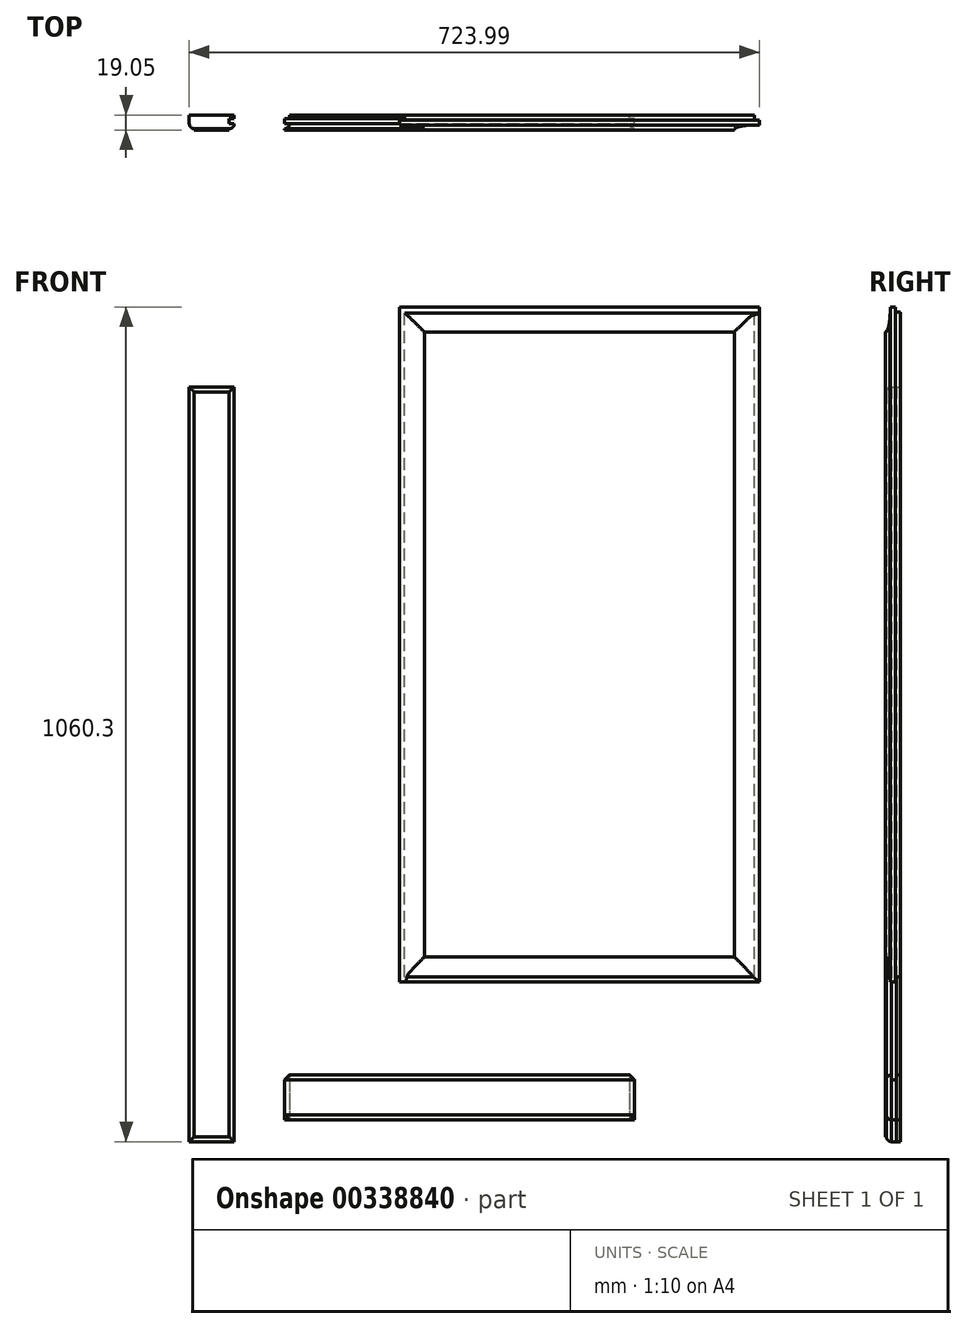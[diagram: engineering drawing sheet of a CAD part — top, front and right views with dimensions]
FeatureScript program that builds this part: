
annotation { "Feature Type Name" : "Feature", "Feature Type Description" : "" }
export const myFeature = defineFeature(function(context is Context, id is Id, definition is map)
    precondition{}
    {
        {
            var Q0;
            Q0=qCreatedBy(makeId("Front.planeOp"),FACE);
            var sketch = newSketch(context, id + "F0", { "sketchPlane" : qUnion([Q0])});
            skLineSegment(sketch, "E0.bottom", {"start": v(-96.9, 637.81) * mm, "end": v(-39.75, 637.81) * mm});
            skLineSegment(sketch, "E0.top", {"start": v(-96.9, -321.04) * mm, "end": v(-39.75, -321.04) * mm});
            skLineSegment(sketch, "E0.left", {"start": v(-96.9, 637.81) * mm, "end": v(-96.9, -321.04) * mm});
            skLineSegment(sketch, "E0.right", {"start": v(-39.75, 637.81) * mm, "end": v(-39.75, -321.04) * mm});
            skSolve(sketch);
        }
        {
            var Q0;
            Q0 = qSketchRegion(id + "F0", true);
            extrude(context, id + "F1", {"entities" : qUnion([Q0]), "depth" : 19.05 * mm});
        }
        {
            var Q0;
            Q0=makeQuery(id+"F1.opExtrude","SWEPT_FACE",FACE,{"disambiguationData":[OSD([sQuery(id+"F0.wireOp",EDGE,"E0.top")])]});
            var sketch = newSketch(context, id + "F2", { "sketchPlane" : qUnion([Q0])});
            skLineSegment(sketch, "E1.0", {"start": v(-46.1, 19.05) * mm, "end": v(-46.1, 0) * mm, "construction": true});
            skLineSegment(sketch, "E2.0", {"start": v(-96.9, 17.46) * mm, "end": v(-39.75, 17.46) * mm, "construction": true});
            skLineSegment(sketch, "E3.0", {"start": v(-96.9, 11.11) * mm, "end": v(-39.75, 11.11) * mm, "construction": true});
            skArc(sketch, "E4", {"start": v(-39.75, 11.11) * mm, "mid": v(-41.6, 15.6) * mm, "end": v(-46.1, 17.46) * mm});
            skLineSegment(sketch, "E5", {"start": v(-46.1, 19.05) * mm, "end": v(-46.1, 17.46) * mm});
            skLineSegment(sketch, "E6.0", {"start": v(-96.9, 4.76) * mm, "end": v(-39.75, 4.76) * mm, "construction": true});
            skLineSegment(sketch, "E7", {"start": v(-39.75, 11.11) * mm, "end": v(-46.1, 11.11) * mm});
            skLineSegment(sketch, "E8", {"start": v(-46.1, 4.76) * mm, "end": v(-39.75, 4.76) * mm});
            skLineSegment(sketch, "E9", {"start": v(-46.1, 4.76) * mm, "end": v(-46.1, 11.11) * mm});
            skLineSegment(sketch, "E10.0", {"start": v(-90.55, 19.05) * mm, "end": v(-90.55, 0) * mm, "construction": true});
            skArc(sketch, "E11", {"start": v(-90.55, 17.46) * mm, "mid": v(-95.04, 15.6) * mm, "end": v(-96.9, 11.11) * mm});
            skLineSegment(sketch, "E12", {"start": v(-90.55, 17.46) * mm, "end": v(-90.55, 19.05) * mm});
            skSolve(sketch);
        }
        {
            var Q0;
            {var subQ0=sQuery(id+"F2.wireOp",EDGE,"E4");Q0=makeQuery(id+"F2.imprint","IMPRINT",FACE,{"disambiguationData":[TD([[makeQuery(id+"F2.imprint","IMPRINT",EDGE,{"derivedFrom":subQ0}),-1.0]])]});}
            extrude(context, id + "F3", {"entities" : qUnion([Q0]), "operationType" : NewBodyOperationType.REMOVE, "oppositeDirection" : true, "depth" : 965.2 * mm});
        }
        {
            var Q0;
            {var subQ0=sQuery(id+"F2.wireOp",EDGE,"E7");Q0=makeQuery(id+"F2.imprint","IMPRINT",FACE,{"disambiguationData":[TD([[makeQuery(id+"F2.imprint","IMPRINT",EDGE,{"derivedFrom":subQ0}),1.0]])]});}
            extrude(context, id + "F4", {"entities" : qUnion([Q0]), "operationType" : NewBodyOperationType.REMOVE, "oppositeDirection" : true, "depth" : 965.2 * mm});
        }
        {
            var Q0;
            {var subQ0=sQuery(id+"F2.wireOp",EDGE,"E11");Q0=makeQuery(id+"F2.imprint","IMPRINT",FACE,{"disambiguationData":[TD([[makeQuery(id+"F2.imprint","IMPRINT",EDGE,{"derivedFrom":subQ0}),-1.0]])]});}
            extrude(context, id + "F5", {"entities" : qUnion([Q0]), "operationType" : NewBodyOperationType.REMOVE, "oppositeDirection" : true, "depth" : 965.2 * mm});
        }
        {
            var Q0;
            Q0=makeQuery(id+"F1.opExtrude","SWEPT_FACE",FACE,{"disambiguationData":[OSD([sQuery(id+"F0.wireOp",EDGE,"E0.left")])]});
            var sketch = newSketch(context, id + "F6", { "sketchPlane" : qUnion([Q0])});
            skLineSegment(sketch, "E13.0", {"start": v(17.46, -314.69) * mm, "end": v(0, -314.69) * mm, "construction": true});
            skArc(sketch, "E14", {"start": v(11.11, -321.04) * mm, "mid": v(15.6, -319.18) * mm, "end": v(17.46, -314.69) * mm});
            skLineSegment(sketch, "E15", {"start": v(11.11, -314.69) * mm, "end": v(11.11, -321.04) * mm, "construction": true});
            skLineSegment(sketch, "E16", {"start": v(17.46, -314.69) * mm, "end": v(19.05, -314.69) * mm});
            skLineSegment(sketch, "E17.0", {"start": v(17.46, 644.16) * mm, "end": v(17.46, -321.04) * mm, "construction": true});
            skLineSegment(sketch, "E18.0", {"start": v(19.05, 637.81) * mm, "end": v(19.05, -321.04) * mm, "construction": true});
            skLineSegment(sketch, "E19", {"start": v(19.05, -314.69) * mm, "end": v(19.05, -321.04) * mm});
            skLineSegment(sketch, "E20", {"start": v(11.11, -321.04) * mm, "end": v(19.05, -321.04) * mm});
            skLineSegment(sketch, "E21.0", {"start": v(19.05, 631.46) * mm, "end": v(0, 631.46) * mm, "construction": true});
            skArc(sketch, "E22", {"start": v(17.46, 631.46) * mm, "mid": v(15.6, 635.95) * mm, "end": v(11.11, 637.81) * mm});
            skLineSegment(sketch, "E23", {"start": v(11.11, 631.46) * mm, "end": v(11.11, 637.81) * mm, "construction": true});
            skLineSegment(sketch, "E24", {"start": v(17.46, 631.46) * mm, "end": v(19.05, 631.46) * mm});
            skLineSegment(sketch, "E25", {"start": v(19.05, 637.81) * mm, "end": v(19.05, 631.46) * mm});
            skLineSegment(sketch, "E26", {"start": v(11.11, 637.81) * mm, "end": v(19.05, 637.81) * mm});
            skLineSegment(sketch, "E27.0", {"start": v(4.76, 637.81) * mm, "end": v(4.76, -321.04) * mm, "construction": true});
            skLineSegment(sketch, "E28", {"start": v(11.11, 637.81) * mm, "end": v(11.11, 631.46) * mm});
            skLineSegment(sketch, "E29", {"start": v(11.11, 631.46) * mm, "end": v(4.76, 631.46) * mm});
            skLineSegment(sketch, "E30", {"start": v(4.76, 631.46) * mm, "end": v(4.76, 637.81) * mm});
            skSolve(sketch);
        }
        {
            var Q0;
            Q0=makeQuery(id+"F6.imprint","IMPRINT",FACE,{"disambiguationData":[TD([[makeQuery(id+"F6.imprint","IMPRINT",EDGE,{"derivedFrom":sQuery(id+"F6.wireOp",EDGE,"E14")}),-1.0]])]});
            extrude(context, id + "F7", {"entities" : qUnion([Q0]), "operationType" : NewBodyOperationType.REMOVE, "oppositeDirection" : true, "depth" : 57.15 * mm});
        }
        {
            var Q0;
            Q0 = qSketchRegion(id + "F6", true);
            extrude(context, id + "F8", {"entities" : qUnion([Q0]), "operationType" : NewBodyOperationType.REMOVE, "oppositeDirection" : true, "depth" : 57.15 * mm});
        }
        {
            var Q0;
            Q0=qCreatedBy(makeId("Front.planeOp"),FACE);
            var sketch = newSketch(context, id + "F9", { "sketchPlane" : qUnion([Q0])});
            skLineSegment(sketch, "E31.bottom", {"start": v(24.23, -236.13) * mm, "end": v(468.73, -236.13) * mm});
            skLineSegment(sketch, "E31.top", {"start": v(24.23, -293.28) * mm, "end": v(468.73, -293.28) * mm});
            skLineSegment(sketch, "E31.left", {"start": v(24.23, -236.13) * mm, "end": v(24.23, -293.28) * mm});
            skLineSegment(sketch, "E31.right", {"start": v(468.73, -236.13) * mm, "end": v(468.73, -293.28) * mm});
            skSolve(sketch);
        }
        {
            var Q0;
            Q0 = qSketchRegion(id + "F9", true);
            extrude(context, id + "F10", {"entities" : qUnion([Q0]), "depth" : 19.05 * mm});
        }
        {
            var Q0;
            Q0=makeQuery(id+"F10.opExtrude","SWEPT_FACE",FACE,{"disambiguationData":[OSD([sQuery(id+"F9.wireOp",EDGE,"E31.right")])]});
            var sketch = newSketch(context, id + "F11", { "sketchPlane" : qUnion([Q0])});
            skLineSegment(sketch, "E32.0", {"start": v(-19.05, -242.48) * mm, "end": v(0, -242.48) * mm, "construction": true});
            skLineSegment(sketch, "E33.0", {"start": v(-19.05, -286.93) * mm, "end": v(0, -286.93) * mm, "construction": true});
            skLineSegment(sketch, "E34.0", {"start": v(-17.46, -236.13) * mm, "end": v(-17.46, -293.28) * mm, "construction": true});
            skLineSegment(sketch, "E35.0", {"start": v(-11.11, -236.13) * mm, "end": v(-11.11, -293.28) * mm, "construction": true});
            skLineSegment(sketch, "E36.0", {"start": v(-4.76, -236.13) * mm, "end": v(-4.76, -293.28) * mm, "construction": true});
            skArc(sketch, "E37", {"start": v(-11.11, -236.13) * mm, "mid": v(-15.6, -237.99) * mm, "end": v(-17.46, -242.48) * mm});
            skArc(sketch, "E38", {"start": v(-17.46, -286.93) * mm, "mid": v(-15.6, -291.42) * mm, "end": v(-11.11, -293.28) * mm});
            skLineSegment(sketch, "E39", {"start": v(-19.05, -242.48) * mm, "end": v(-17.46, -242.48) * mm});
            skLineSegment(sketch, "E40", {"start": v(-11.11, -236.13) * mm, "end": v(-11.11, -242.48) * mm});
            skLineSegment(sketch, "E41", {"start": v(-4.76, -242.48) * mm, "end": v(-11.11, -242.48) * mm});
            skLineSegment(sketch, "E42", {"start": v(-4.76, -242.48) * mm, "end": v(-4.76, -236.13) * mm});
            skLineSegment(sketch, "E43", {"start": v(-19.05, -286.93) * mm, "end": v(-17.46, -286.93) * mm});
            skSolve(sketch);
        }
        {
            var Q0;
            {var subQ0=sQuery(id+"F11.wireOp",EDGE,"E37");Q0=makeQuery(id+"F11.imprint","IMPRINT",FACE,{"disambiguationData":[TD([[makeQuery(id+"F11.imprint","IMPRINT",EDGE,{"derivedFrom":subQ0}),-1.0]])]});}
            var Q1;
            {var subQ0=sQuery(id+"F11.wireOp",EDGE,"E38");Q1=makeQuery(id+"F11.imprint","IMPRINT",FACE,{"disambiguationData":[TD([[makeQuery(id+"F11.imprint","IMPRINT",EDGE,{"derivedFrom":subQ0}),-1.0]])]});}
            var Q2;
            {var subQ0=sQuery(id+"F11.wireOp",EDGE,"E40");Q2=makeQuery(id+"F11.imprint","IMPRINT",FACE,{"disambiguationData":[TD([[makeQuery(id+"F11.imprint","IMPRINT",EDGE,{"derivedFrom":subQ0}),1.0]])]});}
            extrude(context, id + "F12", {"entities" : qUnion([Q0, Q1, Q2]), "operationType" : NewBodyOperationType.REMOVE, "oppositeDirection" : true, "depth" : 444.5 * mm});
        }
        {
            var Q0;
            Q0=makeQuery(id+"F10.opExtrude","SWEPT_FACE",FACE,{"disambiguationData":[OSD([sQuery(id+"F9.wireOp",EDGE,"E31.top")])]});
            var sketch = newSketch(context, id + "F13", { "sketchPlane" : qUnion([Q0])});
            skLineSegment(sketch, "E44.0", {"start": v(30.58, 11.11) * mm, "end": v(30.58, 0) * mm, "construction": true});
            skLineSegment(sketch, "E45.0", {"start": v(24.23, 17.46) * mm, "end": v(468.74, 17.46) * mm, "construction": true});
            skLineSegment(sketch, "E46.0", {"start": v(24.23, 19.05) * mm, "end": v(468.73, 19.05) * mm, "construction": true});
            skLineSegment(sketch, "E47.0", {"start": v(24.23, 4.76) * mm, "end": v(468.74, 4.76) * mm, "construction": true});
            skArc(sketch, "E48", {"start": v(30.58, 11.11) * mm, "mid": v(28.72, 15.6) * mm, "end": v(24.23, 17.46) * mm});
            skLineSegment(sketch, "E49", {"start": v(24.23, 17.46) * mm, "end": v(24.23, 19.05) * mm});
            skLineSegment(sketch, "E50", {"start": v(30.58, 11.11) * mm, "end": v(24.23, 11.11) * mm});
            skLineSegment(sketch, "E51", {"start": v(24.23, 4.76) * mm, "end": v(30.58, 4.76) * mm});
            skLineSegment(sketch, "E52", {"start": v(30.58, 4.76) * mm, "end": v(30.58, 0) * mm});
            skLineSegment(sketch, "E53", {"start": v(24.23, 17.46) * mm, "end": v(24.23, 11.11) * mm});
            skLineSegment(sketch, "E54.0", {"start": v(462.38, 11.11) * mm, "end": v(462.38, 0) * mm, "construction": true});
            skArc(sketch, "E55", {"start": v(468.74, 17.46) * mm, "mid": v(464.24, 15.6) * mm, "end": v(462.38, 11.11) * mm});
            skArc(sketch, "E56.trimOffspring", {"start": v(468.72, 4.76) * mm, "mid": v(468.73, 4.76) * mm, "end": v(468.74, 4.76) * mm});
            skLineSegment(sketch, "E57", {"start": v(468.74, 17.46) * mm, "end": v(468.73, 11.11) * mm});
            skLineSegment(sketch, "E58", {"start": v(468.74, 4.76) * mm, "end": v(462.38, 4.76) * mm});
            skLineSegment(sketch, "E59", {"start": v(462.38, 4.76) * mm, "end": v(462.38, 0) * mm});
            skSolve(sketch);
        }
        {
            var Q0;
            Q0=makeQuery(id+"F13.imprint","IMPRINT",FACE,{"disambiguationData":[TD([[makeQuery(id+"F13.imprint","IMPRINT",EDGE,{"derivedFrom":sQuery(id+"F13.wireOp",EDGE,"E48")}),1.0]])]});
            var Q1;
            {var subQ0=sQuery(id+"F13.wireOp",EDGE,"E51");Q1=makeQuery(id+"F13.imprint","IMPRINT",FACE,{"disambiguationData":[TD([[makeQuery(id+"F13.imprint","IMPRINT",EDGE,{"derivedFrom":subQ0}),-1.0]])]});}
            extrude(context, id + "F14", {"entities" : qUnion([Q0, Q1]), "operationType" : NewBodyOperationType.REMOVE, "oppositeDirection" : true, "depth" : 57.15 * mm});
        }
        {
            var Q0;
            {var subQ6=sQuery(id+"F13.wireOp",EDGE,"E56.trimOffspring");Q0=makeQuery(id+"F13.imprint","IMPRINT",FACE,{"disambiguationData":[TD([[makeQuery(id+"F13.imprint","IMPRINT",EDGE,{"derivedFrom":subQ6}),-1.0]])]});}
            var Q1;
            {var subQ0=sQuery(id+"F13.wireOp",EDGE,"E55");Q1=makeQuery(id+"F13.imprint","IMPRINT",FACE,{"disambiguationData":[TD([[makeQuery(id+"F13.imprint","IMPRINT",EDGE,{"derivedFrom":subQ0}),1.0]])]});}
            extrude(context, id + "F15", {"entities" : qUnion([Q0, Q1]), "operationType" : NewBodyOperationType.REMOVE, "oppositeDirection" : true, "depth" : 57.15 * mm});
        }
        {
            var Q0;
            Q0=qCreatedBy(makeId("Front.planeOp"),FACE);
            var sketch = newSketch(context, id + "F16", { "sketchPlane" : qUnion([Q0])});
            skLineSegment(sketch, "E60.bottom", {"start": v(169.89, 739.26) * mm, "end": v(627.09, 739.26) * mm});
            skLineSegment(sketch, "E60.top", {"start": v(169.89, -118) * mm, "end": v(627.09, -118) * mm});
            skLineSegment(sketch, "E60.left", {"start": v(169.89, 739.26) * mm, "end": v(169.89, -118) * mm});
            skLineSegment(sketch, "E60.right", {"start": v(627.09, 739.26) * mm, "end": v(627.09, -118) * mm});
            skSolve(sketch);
        }
        {
            var Q0;
            Q0 = qSketchRegion(id + "F16", true);
            extrude(context, id + "F17", {"entities" : qUnion([Q0]), "depth" : 19.05 * mm});
        }
        {
            var Q0;
            Q0=makeQuery(id+"F17.opExtrude","SWEPT_FACE",FACE,{"disambiguationData":[OSD([sQuery(id+"F16.wireOp",EDGE,"E60.bottom")])]});
            var sketch = newSketch(context, id + "F18", { "sketchPlane" : qUnion([Q0])});
            skLineSegment(sketch, "E61.0", {"start": v(620.74, -19.05) * mm, "end": v(620.74, 0) * mm, "construction": true});
            skLineSegment(sketch, "E62.0", {"start": v(169.89, -6.35) * mm, "end": v(627.09, -6.35) * mm, "construction": true});
            skLineSegment(sketch, "E63.0", {"start": v(169.89, -12.7) * mm, "end": v(627.09, -12.7) * mm, "construction": true});
            skLineSegment(sketch, "E64.0", {"start": v(595.34, -19.05) * mm, "end": v(595.34, 0) * mm, "construction": true});
            skEllipticalArc(sketch, "E65", {});
            skLineSegment(sketch, "E66", {"start": v(620.74, -12.75) * mm, "end": v(627.09, -12.7) * mm});
            skLineSegment(sketch, "E67", {"start": v(627.09, -6.35) * mm, "end": v(627.09, -12.7) * mm});
            skLineSegment(sketch, "E68", {"start": v(620.74, -6.35) * mm, "end": v(627.09, -6.35) * mm});
            skLineSegment(sketch, "E69", {"start": v(620.74, 0) * mm, "end": v(620.74, -6.35) * mm});
            skLineSegment(sketch, "E70.0", {"start": v(176.24, -19.05) * mm, "end": v(176.24, 0) * mm, "construction": true});
            skLineSegment(sketch, "E71.0", {"start": v(201.64, -19.05) * mm, "end": v(201.64, 0) * mm, "construction": true});
            skEllipticalArc(sketch, "E72", {});
            skLineSegment(sketch, "E73", {"start": v(176.24, -12.7) * mm, "end": v(169.89, -12.7) * mm});
            skLineSegment(sketch, "E74", {"start": v(169.89, -6.35) * mm, "end": v(169.89, -12.7) * mm});
            skLineSegment(sketch, "E75", {"start": v(176.24, -6.35) * mm, "end": v(169.89, -6.35) * mm});
            skLineSegment(sketch, "E76", {"start": v(176.24, -6.35) * mm, "end": v(176.24, 0) * mm});
            const initialGuessF18  = {"E65": [0.6207356769722712, -0.01905, -1, 0, 0.0254, 0.006295941264803342, 4.71238898038469, 0], "E72": [0.1762356727045784, -0.01905, 1, 0, 0.0254, 0.006353643925652308, 0, 1.5707963267948966]};
            skSetInitialGuess(sketch, initialGuessF18);
            skSolve(sketch);
        }
        {
            var Q0;
            {var subQ0=sQuery(id+"F18.wireOp",EDGE,"E65");Q0=makeQuery(id+"F18.imprint","IMPRINT",FACE,{"disambiguationData":[TD([[makeQuery(id+"F18.imprint","IMPRINT",EDGE,{"derivedFrom":subQ0}),1.0]])]});}
            var Q1;
            {var subQ0=sQuery(id+"F18.wireOp",EDGE,"E68");Q1=makeQuery(id+"F18.imprint","IMPRINT",FACE,{"disambiguationData":[TD([[makeQuery(id+"F18.imprint","IMPRINT",EDGE,{"derivedFrom":subQ0}),1.0]])]});}
            extrude(context, id + "F19", {"entities" : qUnion([Q0, Q1]), "operationType" : NewBodyOperationType.REMOVE, "oppositeDirection" : true, "depth" : 863.6 * mm});
        }
        {
            var Q0;
            {var subQ0=sQuery(id+"F18.wireOp",EDGE,"E72");Q0=makeQuery(id+"F18.imprint","IMPRINT",FACE,{"disambiguationData":[TD([[makeQuery(id+"F18.imprint","IMPRINT",EDGE,{"derivedFrom":subQ0}),1.0]])]});}
            var Q1;
            {var subQ0=sQuery(id+"F18.wireOp",EDGE,"E75");Q1=makeQuery(id+"F18.imprint","IMPRINT",FACE,{"disambiguationData":[TD([[makeQuery(id+"F18.imprint","IMPRINT",EDGE,{"derivedFrom":subQ0}),-1.0]])]});}
            extrude(context, id + "F20", {"entities" : qUnion([Q0, Q1]), "operationType" : NewBodyOperationType.REMOVE, "oppositeDirection" : true, "depth" : 863.6 * mm});
        }
        {
            var Q0;
            Q0=makeQuery(id+"F17.opExtrude","SWEPT_FACE",FACE,{"disambiguationData":[OSD([sQuery(id+"F16.wireOp",EDGE,"E60.right")])]});
            var sketch = newSketch(context, id + "F21", { "sketchPlane" : qUnion([Q0])});
            skLineSegment(sketch, "E77.0", {"start": v(-19.05, -111.64) * mm, "end": v(0, -111.64) * mm, "construction": true});
            skLineSegment(sketch, "E78.0", {"start": v(-19.05, -86.24) * mm, "end": v(-6.35, -86.24) * mm, "construction": true});
            skLineSegment(sketch, "E79.0", {"start": v(0, -118) * mm, "end": v(0, 739.26) * mm, "construction": true});
            skLineSegment(sketch, "E80.0", {"start": v(-19.05, -118) * mm, "end": v(-19.05, 745.6) * mm, "construction": true});
            skEllipticalArc(sketch, "E81", {});
            skLineSegment(sketch, "E82", {"start": v(-12.77, -111.64) * mm, "end": v(-12.7, -118) * mm});
            skLineSegment(sketch, "E83", {"start": v(-12.7, -118) * mm, "end": v(-6.35, -118) * mm});
            skLineSegment(sketch, "E84", {"start": v(-6.35, -118) * mm, "end": v(-6.35, -111.64) * mm});
            skLineSegment(sketch, "E85", {"start": v(-6.35, -111.64) * mm, "end": v(0, -111.64) * mm});
            skLineSegment(sketch, "E86", {"start": v(0, -111.64) * mm, "end": v(0, -118) * mm});
            skLineSegment(sketch, "E87", {"start": v(0, -118) * mm, "end": v(-6.35, -118) * mm});
            skLineSegment(sketch, "E88", {"start": v(-12.7, -118) * mm, "end": v(-19.05, -118) * mm});
            skLineSegment(sketch, "E89", {"start": v(-19.05, -118) * mm, "end": v(-19.05, -86.24) * mm});
            skLineSegment(sketch, "E90.0", {"start": v(-19.05, 732.9) * mm, "end": v(0, 732.9) * mm, "construction": true});
            skLineSegment(sketch, "E91.0", {"start": v(-19.05, 707.5) * mm, "end": v(0, 707.5) * mm, "construction": true});
            skEllipticalArc(sketch, "E92", {});
            skLineSegment(sketch, "E93", {"start": v(-19.05, 707.5) * mm, "end": v(-19.05, 745.6) * mm});
            skLineSegment(sketch, "E94", {"start": v(-12.7, 739.26) * mm, "end": v(-12.69, 732.9) * mm});
            skLineSegment(sketch, "E95", {"start": v(-6.35, 739.26) * mm, "end": v(-6.35, 732.9) * mm});
            skLineSegment(sketch, "E96", {"start": v(-6.35, 732.9) * mm, "end": v(0, 732.9) * mm});
            skLineSegment(sketch, "E97", {"start": v(0, 739.26) * mm, "end": v(0, 732.9) * mm});
            skLineSegment(sketch, "E98", {"start": v(0, 739.26) * mm, "end": v(-6.35, 739.26) * mm});
            skLineSegment(sketch, "E99", {"start": v(-12.7, 739.26) * mm, "end": v(-19.05, 745.6) * mm});
            skLineSegment(sketch, "E100", {"start": v(0, -118) * mm, "end": v(0, -111.64) * mm});
            skLineSegment(sketch, "E101", {"start": v(-6.35, -111.64) * mm, "end": v(-6.35, -118) * mm});
            const initialGuessF21  = {"E81": [-0.01904999984651804, -0.11164165569543845, 0, 1, 0.0254, 0.006283176488403172, 4.71238898038469, 0], "E92": [-0.01904999984651804, 0.7329083443045618, 0, -1, 0.0254, 0.0063606174153418, 0, 1.5707963267948966]};
            skSetInitialGuess(sketch, initialGuessF21);
            skSolve(sketch);
        }
        {
            var Q0;
            Q0=makeQuery(id+"F21.imprint","IMPRINT",FACE,{"disambiguationData":[TD([[makeQuery(id+"F21.imprint","IMPRINT",EDGE,{"derivedFrom":sQuery(id+"F21.wireOp",EDGE,"E81")}),1.0]])]});
            var Q1;
            Q1=makeQuery(id+"F21.imprint","IMPRINT",FACE,{"disambiguationData":[TD([[makeQuery(id+"F21.imprint","IMPRINT",EDGE,{"derivedFrom":sQuery(id+"F21.wireOp",EDGE,"E84")}),-1.0]])]});
            extrude(context, id + "F22", {"entities" : qUnion([Q0, Q1]), "operationType" : NewBodyOperationType.REMOVE, "oppositeDirection" : true, "depth" : 457.2 * mm});
        }
        {
            var Q0;
            {var subQ0=sQuery(id+"F21.wireOp",EDGE,"E93");Q0=makeQuery(id+"F21.imprint","IMPRINT",FACE,{"disambiguationData":[TD([[makeQuery(id+"F21.imprint","IMPRINT",EDGE,{"derivedFrom":subQ0}),-1.0]])]});}
            var Q1;
            Q1=makeQuery(id+"F21.imprint","IMPRINT",FACE,{"disambiguationData":[TD([[makeQuery(id+"F21.imprint","IMPRINT",EDGE,{"derivedFrom":sQuery(id+"F21.wireOp",EDGE,"E95")}),-1.0]])]});
            extrude(context, id + "F23", {"entities" : qUnion([Q0, Q1]), "operationType" : NewBodyOperationType.REMOVE, "oppositeDirection" : true, "depth" : 457.2 * mm});
        }
        {
            var Q0;
            Q0=makeQuery(id+"F21.imprint","IMPRINT",FACE,{"disambiguationData":[TD([[makeQuery(id+"F21.imprint","IMPRINT",EDGE,{"derivedFrom":sQuery(id+"F21.wireOp",EDGE,"E85")}),-1.0]])]});
            extrude(context, id + "F24", {"entities" : qUnion([Q0]), "operationType" : NewBodyOperationType.REMOVE, "oppositeDirection" : true, "depth" : 457.2 * mm});
        }
    });
